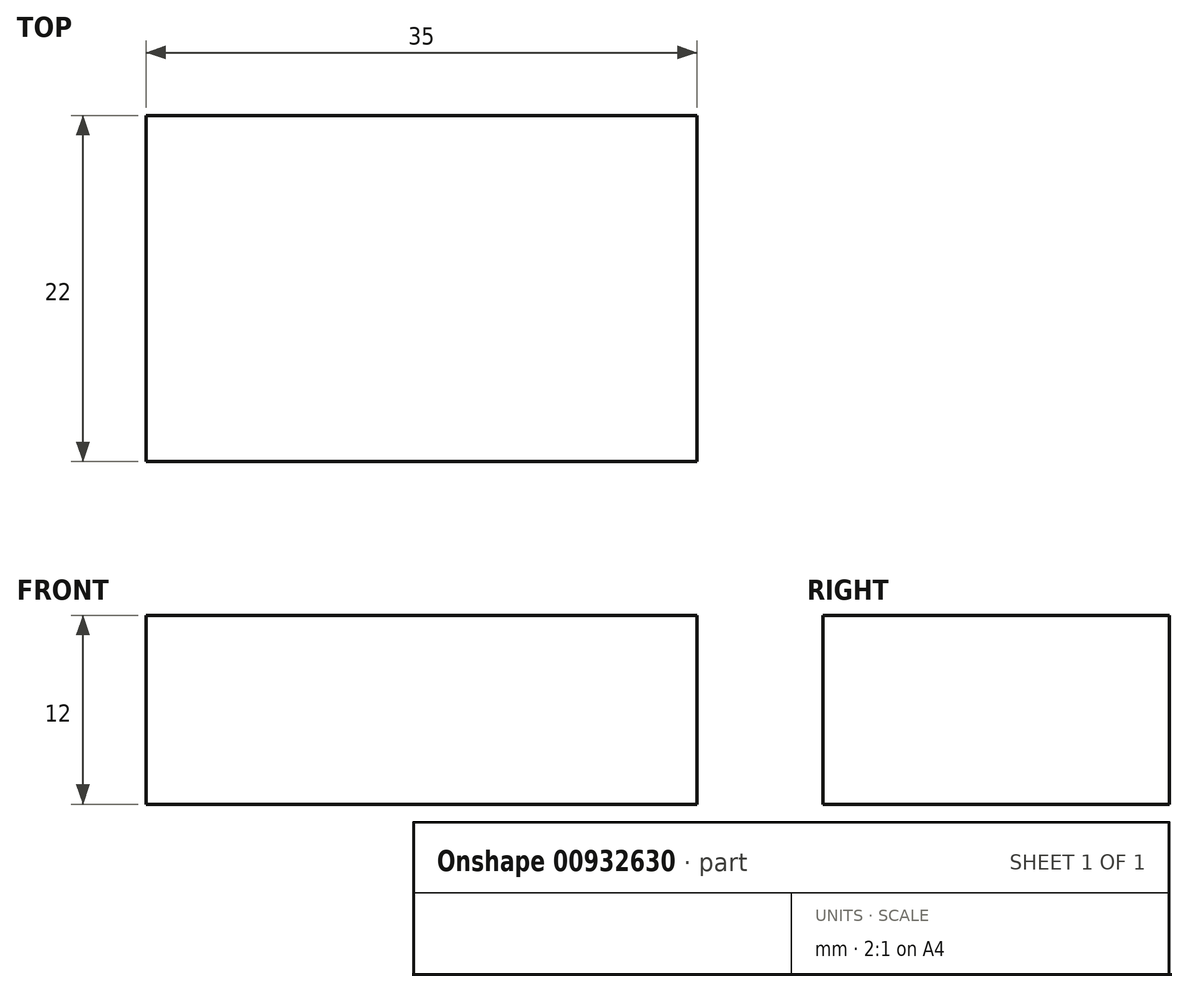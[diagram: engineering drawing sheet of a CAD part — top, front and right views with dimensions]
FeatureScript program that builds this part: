
annotation { "Feature Type Name" : "Feature", "Feature Type Description" : "" }
export const myFeature = defineFeature(function(context is Context, id is Id, definition is map)
    precondition{}
    {
        {
            var Q0;
            Q0=qCreatedBy(makeId("Top.planeOp"),FACE);
            var sketch = newSketch(context, id + "F0", { "sketchPlane" : qUnion([Q0])});
            skLineSegment(sketch, "E0.bottom", {"start": v(17.5, -11) * mm, "end": v(-17.5, -11) * mm});
            skLineSegment(sketch, "E0.top", {"start": v(17.5, 11) * mm, "end": v(-17.5, 11) * mm});
            skLineSegment(sketch, "E0.left", {"start": v(17.5, -11) * mm, "end": v(17.5, 11) * mm});
            skLineSegment(sketch, "E0.right", {"start": v(-17.5, -11) * mm, "end": v(-17.5, 11) * mm});
            skPoint(sketch, "E0.middle", {"position": v(0, 0) * mm});
            skSolve(sketch);
        }
        {
            var Q0;
            Q0 = qSketchRegion(id + "F0", true);
            extrude(context, id + "F1", {"entities" : qUnion([Q0]), "depth" : 12 * mm, "offsetDistance" : 25 * mm});
        }
    });
